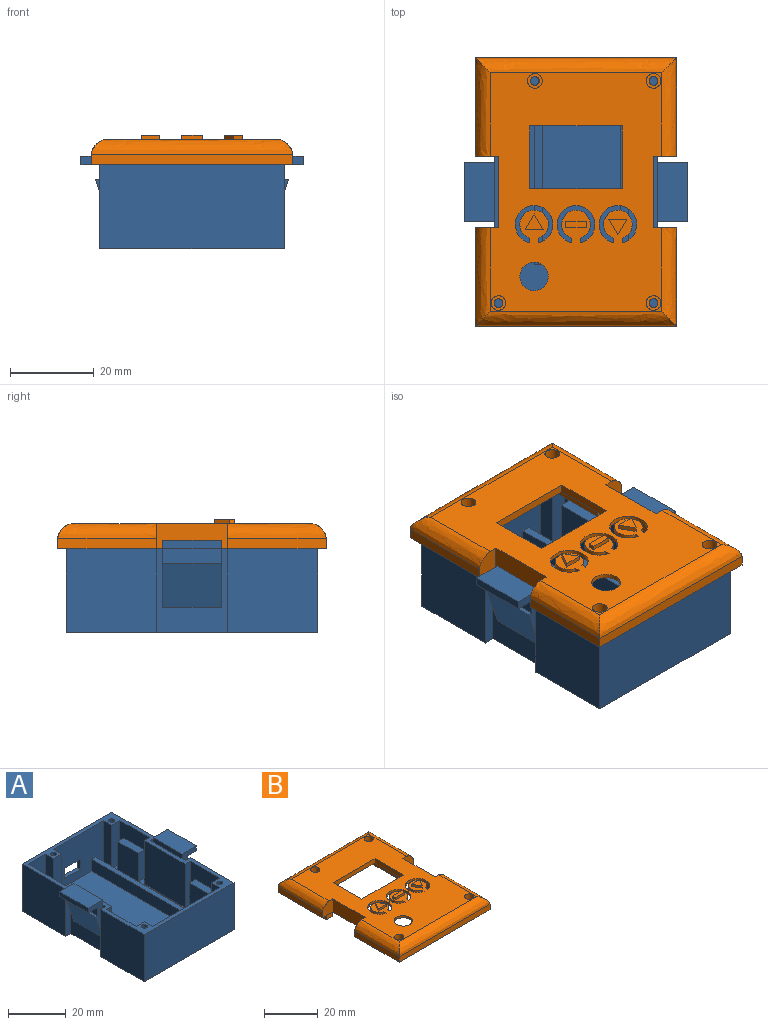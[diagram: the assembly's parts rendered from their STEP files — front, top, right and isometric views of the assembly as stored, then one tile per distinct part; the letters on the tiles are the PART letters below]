
ASSEMBLY  parts=2 mates=1
PART A: 93 faces, bbox 53x60x22 mm
  f0: plane 6x5mm, normal (0,1,0), area 30mm2, adj f2,f9,f73,f91
  f1: plane 8x5mm, normal (0,-1,0), area 40mm2, adj f2,f9,f77,f91
  f2: plane 45.7x8mm, normal (0,0,1), area 103.4mm2, adj f0,f1,f6,f73,f77,f91
  f3: plane 18.5x14.5mm, normal (-1,0,0), area 148.3mm2, adj f9,f18,f34,f56,f83,f84,f86
  f4: plane 18.5x14.5mm, normal (-1,0,0), area 148.2mm2, adj f9,f18,f35,f54,f79,f80,f82
  f5: plane 18.5x4mm, normal (0,-1,0), area 64mm2, adj f9,f18,f59,f60,f75,f78
  f6: plane 24.5x18.5mm, normal (0,-1,0), area 410.9mm2, adj f2,f9,f18,f53,f59,f69,f70,f71
  f7: plane 44x20mm, normal (0,1,0), area 847.7mm2, adj f17,f18,f21,f23,f69,f70,f71,f72
  f8: plane 20x8.5mm, normal (0,-1,0), area 164.7mm2, adj f9,f17,f18,f30,f38,f39,f60
  f9: plane 57x41mm, normal (0,0,1), area 1808mm2, adj f0,f1,f3,f4,f5,f6,f8,f10
  f10: plane 18.5x14.5mm, normal (1,0,0), area 148.3mm2, adj f9,f18,f31,f58,f87,f89,f90
  f11: plane 33x18.5mm, normal (0,1,0), area 610.5mm2, adj f9,f18,f55,f57
  f12: plane 14x2mm, normal (-1,0,0), area 28mm2, adj f13,f14,f47,f49
  f13: plane 16x7mm, normal (0,-1,0), area 41.1mm2, adj f12,f25,f47,f48,f49,f50,f51,f52
  f14: plane 16x7mm, normal (0,1,0), area 41.1mm2, adj f12,f25,f47,f48,f49,f50,f51,f52
  f15: plane 16x7mm, normal (0,-1,0), area 41.1mm2, adj f29,f40,f41,f42,f43,f44,f45,f46
  f16: plane 16x7mm, normal (0,1,0), area 41.1mm2, adj f29,f40,f41,f42,f43,f44,f45,f46
  f17: plane 60x44mm, normal (0,0,-1), area 2480mm2, adj f7,f8,f19,f20,f21,f22,f23,f24
  f18: plane 60x44mm, normal (0,0,1), area 368.1mm2, adj f3,f4,f5,f6,f7,f8,f10,f11
  f19: plane 21.5x20mm, normal (-1,0,0), area 430mm2, adj f17,f18,f22,f24
  f20: plane 21.5x20mm, normal (1,0,0), area 430mm2, adj f17,f18,f22,f27
  f21: plane 21.5x20mm, normal (-1,0,0), area 430mm2, adj f7,f17,f18,f26
  f22: plane 44x20mm, normal (0,-1,0), area 880mm2, adj f17,f18,f19,f20
  f23: plane 21.5x20mm, normal (1,0,0), area 430mm2, adj f7,f17,f18,f28
  f24: plane 20x2.5mm, normal (0,1,0), area 50mm2, adj f17,f18,f19,f25
  f25: plane 20x17mm, normal (-1,0,0), area 144mm2, adj f13,f14,f17,f18,f24,f26,f50
  f26: plane 20x2.5mm, normal (0,-1,0), area 50mm2, adj f17,f18,f21,f25
  f27: plane 20x2.5mm, normal (0,1,0), area 50mm2, adj f17,f18,f20,f29
  f28: plane 20x2.5mm, normal (0,-1,0), area 50mm2, adj f17,f18,f23,f29
  f29: plane 20x17mm, normal (1,0,0), area 144mm2, adj f15,f16,f17,f18,f27,f28,f46
  f30: plane 18.5x18.5mm, normal (1,0,0), area 342.3mm2, adj f8,f9,f18,f33
  f31: plane 18.5x2.5mm, normal (0,-1,0), area 46.3mm2, adj f9,f10,f18,f32
  f32: plane 20x18.5mm, normal (1,0,0), area 370mm2, adj f9,f18,f31,f33
  f33: plane 18.5x2.5mm, normal (0,1,0), area 46.3mm2, adj f9,f18,f30,f32
  f34: plane 18.5x2.5mm, normal (0,-1,0), area 46.3mm2, adj f3,f9,f18,f36
  f35: plane 18.5x2.5mm, normal (0,1,0), area 46.3mm2, adj f4,f9,f18,f36
  f36: plane 20x18.5mm, normal (-1,0,0), area 370mm2, adj f9,f18,f34,f35
  f37: plane 5x1.5mm, normal (0,1,0), area 7.5mm2, adj f9,f17,f38,f39
  f38: plane 15x1.5mm, normal (1,0,0), area 22.5mm2, adj f8,f9,f17,f37
  f39: plane 15x1.5mm, normal (-1,0,0), area 22.5mm2, adj f8,f9,f17,f37
  f40: plane 14x2mm, normal (-1,0,0), area 28mm2, adj f15,f16,f18,f41
  f41: plane 14x7mm, normal (0,0,1), area 98mm2, adj f15,f16,f40,f42
  f42: plane 14x2mm, normal (1,0,0), area 28mm2, adj f15,f16,f41,f43
  f43: plane 14x4.5mm, normal (0,0,-1), area 63mm2, adj f15,f16,f42,f44
  f44: plane 14x3.5mm, normal (1,0,0), area 49mm2, adj f15,f16,f43,f45
  f45: plane 14x1mm, normal (0,0,1), area 14mm2, adj f15,f16,f44,f46
  f46: plane 14x10.5mm, normal (0.95,0,-0.32), area 155mm2, adj f15,f16,f29,f45
  f47: plane 14x7mm, normal (0,0,1), area 98mm2, adj f12,f13,f14,f48
  f48: plane 14x2mm, normal (1,0,0), area 28mm2, adj f13,f14,f18,f47
  f49: plane 14x4.5mm, normal (0,0,-1), area 63mm2, adj f12,f13,f14,f52
  f50: plane 14x10.5mm, normal (-0.95,0,-0.32), area 155mm2, adj f13,f14,f25,f51
  f51: plane 14x1mm, normal (0,0,1), area 14mm2, adj f13,f14,f50,f52
  f52: plane 14x3.5mm, normal (-1,0,0), area 49mm2, adj f13,f14,f49,f51
  f53: plane 18.5x4mm, normal (-1,0,0), area 74mm2, adj f6,f9,f18,f54
  f54: plane 18.5x4mm, normal (0,-1,0), area 74mm2, adj f4,f9,f18,f53
  f55: plane 18.5x4mm, normal (-1,0,0), area 74mm2, adj f9,f11,f18,f56
  f56: plane 18.5x4mm, normal (0,1,0), area 74mm2, adj f3,f9,f18,f55
  f57: plane 18.5x4mm, normal (1,0,0), area 74mm2, adj f9,f11,f18,f58
  f58: plane 18.5x4mm, normal (0,1,0), area 74mm2, adj f9,f10,f18,f57
  f59: plane 43.7x18.5mm, normal (1,0,0), area 272.5mm2, adj f5,f6,f9,f18,f74,f78
  f60: plane 18.5x4mm, normal (-1,0,0), area 74mm2, adj f5,f8,f9,f18
  f61: cylinder r=1.05mm len=15mm, axis (0,0,1), area 99mm2, adj f18,f62
  f62: plane 2.1x2.1mm, normal (0,0,1), area 3.5mm2, adj f61
  f63: cylinder r=1.05mm len=15mm, axis (0,0,1), area 99mm2, adj f18,f64
  f64: plane 2.1x2.1mm, normal (0,0,1), area 3.5mm2, adj f63
  f65: cylinder r=1.05mm len=15mm, axis (0,0,1), area 99mm2, adj f18,f66
  f66: plane 2.1x2.1mm, normal (0,0,1), area 3.5mm2, adj f65
  f67: cylinder r=1.05mm len=15mm, axis (0,0,1), area 99mm2, adj f18,f68
  f68: plane 2.1x2.1mm, normal (0,0,1), area 3.5mm2, adj f67
  f69: plane 4.2x1.5mm, normal (1,0,0), area 6.3mm2, adj f6,f7,f70,f71
  f70: plane 7.7x1.5mm, normal (0,0,-1), area 11.5mm2, adj f6,f7,f69,f72
  f71: plane 7.7x1.5mm, normal (0,0,1), area 11.5mm2, adj f6,f7,f69,f72
  f72: plane 4.2x1.5mm, normal (-1,0,0), area 6.3mm2, adj f6,f7,f70,f71
  f73: plane 43.7x5mm, normal (-1,0,0), area 218.5mm2, adj f0,f2,f6,f9
  f74: plane 6.6x5mm, normal (0,1,0), area 33mm2, adj f9,f59,f78,f92
  f75: plane 41.7x5mm, normal (-1,0,0), area 208.5mm2, adj f5,f9,f76,f78
  f76: plane 8.6x5mm, normal (0,-1,0), area 43mm2, adj f9,f75,f78,f92
  f77: plane 45.7x5mm, normal (1,0,0), area 228.5mm2, adj f1,f2,f6,f9
  f78: plane 41.7x8.6mm, normal (0,0,1), area 96.6mm2, adj f5,f59,f74,f75,f76,f92
  f79: plane 12x3mm, normal (0,-1,0), area 36mm2, adj f4,f9,f81,f82
  f80: plane 12x3mm, normal (0,1,0), area 36mm2, adj f4,f9,f81,f82
  f81: plane 12x10mm, normal (-1,0,0), area 120mm2, adj f9,f79,f80,f82
  f82: plane 10x3mm, normal (0,0,1), area 30mm2, adj f4,f79,f80,f81
  f83: plane 12x3mm, normal (0,-1,0), area 36mm2, adj f3,f9,f85,f86
  f84: plane 12x3mm, normal (0,1,0), area 36mm2, adj f3,f9,f85,f86
  f85: plane 12x10mm, normal (-1,0,0), area 120mm2, adj f9,f83,f84,f86
  f86: plane 10x3mm, normal (0,0,1), area 30mm2, adj f3,f83,f84,f85
  f87: plane 12x3mm, normal (0,-1,0), area 36mm2, adj f9,f10,f88,f90
  f88: plane 12x10mm, normal (1,0,0), area 120mm2, adj f9,f87,f89,f90
  f89: plane 12x3mm, normal (0,1,0), area 36mm2, adj f9,f10,f88,f90
  f90: plane 10x3mm, normal (0,0,1), area 30mm2, adj f10,f87,f88,f89
  f91: plane 5x2mm, normal (-1,0,0), area 10mm2, adj f0,f1,f2,f9
  f92: plane 5x2mm, normal (1,0,0), area 10mm2, adj f9,f74,f76,f78
PART B: 131 faces, bbox 53.2x66.8x10.9 mm
  f0: plane 50.6x34.6mm, normal (0,0,-1), area 1144.6mm2, adj f53,f54,f55,f56,f57,f58,f59,f60
  f1: plane 2.5x0.24mm, normal (0,0,-1), area 0.4mm2, adj f85,f103
  f2: plane 2.5x0.24mm, normal (0,0,-1), area 0.4mm2, adj f85,f101
  f3: plane 6.32x2.15mm, normal (0,0,-1), area 9.9mm2, adj f85,f102
  f4: plane 2.5x0.24mm, normal (0,0,-1), area 0.4mm2, adj f82,f98
  f5: plane 2.5x0.24mm, normal (0,0,-1), area 0.4mm2, adj f82,f96
  f6: plane 6.32x2.15mm, normal (0,0,-1), area 9.9mm2, adj f82,f97
  f7: plane 2.5x0.24mm, normal (0,0,-1), area 0.4mm2, adj f89,f93
  f8: plane 2.5x0.24mm, normal (0,0,-1), area 0.4mm2, adj f89,f91
  f9: plane 6.32x2.15mm, normal (0,0,-1), area 9.9mm2, adj f89,f92
  f10: plane 57x41mm, normal (0,0,1), area 1765.2mm2, adj f36,f37,f38,f39,f40,f41,f68,f70
  f11: cylinder r=1.05mm len=2.1mm, axis (0,0,-1), area 6.6mm2, adj f19,f73
  f12: cylinder r=1.05mm len=2.1mm, axis (0,0,-1), area 6.6mm2, adj f19,f71
  f13: cylinder r=1.05mm len=2.1mm, axis (0,0,-1), area 6.6mm2, adj f19,f69
  f14: cylinder r=1.05mm len=2.1mm, axis (0,0,-1), area 6.6mm2, adj f19,f67
  f15: plane 3.5x3.1mm, normal (-1,0,0), area 10.9mm2, adj f19,f29,f45,f64
  f16: plane 3.5x3.1mm, normal (0,1,0), area 10.9mm2, adj f19,f25,f47,f53
  f17: plane 3.5x3.1mm, normal (1,0,0), area 10.9mm2, adj f19,f26,f50,f57
  f18: plane 3.5x3.1mm, normal (0,-1,0), area 10.9mm2, adj f19,f27,f52,f54
  f19: plane 64x48mm, normal (0,0,-1), area 746.6mm2, adj f11,f12,f13,f14,f15,f16,f17,f18
  f20: plane 3.5x3.1mm, normal (0,-1,0), area 10.9mm2, adj f19,f28,f42,f54
  f21: plane 3.5x3.1mm, normal (0,-1,0), area 10.9mm2, adj f19,f25,f47,f53
  f22: plane 3.5x3.1mm, normal (0,1,0), area 10.9mm2, adj f19,f24,f48,f53
  f23: plane 3.5x3.1mm, normal (0,1,0), area 10.9mm2, adj f19,f27,f52,f54
  f24: plane 14.2x3.1mm, normal (0,0,-1), area 44mm2, adj f22,f48,f49,f53
  f25: plane 14.2x3.1mm, normal (0,0,-1), area 44mm2, adj f16,f21,f47,f53
  f26: plane 32.6x3.1mm, normal (0,0,-1), area 101.1mm2, adj f17,f50,f51,f57
  f27: plane 14.2x3.1mm, normal (0,0,-1), area 44mm2, adj f18,f23,f52,f54
  f28: plane 18.3x8.5mm, normal (0,0,-1), area 73.5mm2, adj f20,f42,f43,f44,f54,f60
  f29: plane 24x3.1mm, normal (0,0,-1), area 74.4mm2, adj f15,f45,f46,f64
  f30: plane 23.5x2.5mm, normal (1,0,0), area 58.8mm2, adj f19,f32,f36,f124
  f31: plane 23.5x2.5mm, normal (-1,0,0), area 58.8mm2, adj f19,f32,f39,f126
  f32: plane 48x2.5mm, normal (0,-1,0), area 120mm2, adj f19,f30,f31,f125
  f33: plane 23.5x2.5mm, normal (1,0,0), area 58.7mm2, adj f19,f34,f37,f127
  f34: plane 48x2.5mm, normal (0,1,0), area 120mm2, adj f19,f33,f35,f129
  f35: plane 23.5x2.5mm, normal (-1,0,0), area 58.7mm2, adj f19,f34,f41,f128
  f36: plane 6.43x5.93mm, normal (0,1,0), area 29.7mm2, adj f10,f19,f30,f38,f124
  f37: plane 6.43x5.93mm, normal (0,-1,0), area 29.7mm2, adj f10,f19,f33,f38,f127
  f38: plane 17x6mm, normal (1,0,0), area 102mm2, adj f10,f19,f36,f37
  f39: plane 6.43x5.93mm, normal (0,1,0), area 29.7mm2, adj f10,f19,f31,f40,f126
  f40: plane 17x6mm, normal (-1,0,0), area 102mm2, adj f10,f19,f39,f41
  f41: plane 6.43x5.93mm, normal (0,-1,0), area 29.7mm2, adj f10,f19,f35,f40,f128
  f42: plane 18.3x3.5mm, normal (-1,0,0), area 64.1mm2, adj f19,f20,f28,f43
  f43: plane 8.5x3.5mm, normal (0,1,0), area 29.8mm2, adj f19,f28,f42,f44
  f44: plane 3.5x3.1mm, normal (1,0,0), area 10.9mm2, adj f19,f28,f43,f60
  f45: plane 24x3.5mm, normal (0,1,0), area 84mm2, adj f15,f19,f29,f46
  f46: plane 3.5x3.1mm, normal (1,0,0), area 10.9mm2, adj f19,f29,f45,f64
  f47: plane 14.2x3.5mm, normal (1,0,0), area 49.7mm2, adj f16,f19,f21,f25
  f48: plane 14.2x3.5mm, normal (1,0,0), area 49.7mm2, adj f19,f22,f24,f49
  f49: plane 3.5x3.1mm, normal (0,-1,0), area 10.9mm2, adj f19,f24,f48,f53
  f50: plane 32.6x3.5mm, normal (0,-1,0), area 114.1mm2, adj f17,f19,f26,f51
  f51: plane 3.5x3.1mm, normal (-1,0,0), area 10.9mm2, adj f19,f26,f50,f57
  f52: plane 14.2x3.5mm, normal (-1,0,0), area 49.7mm2, adj f18,f19,f23,f27
  f53: plane 48.6x8.5mm, normal (-1,0,0), area 342.4mm2, adj f0,f16,f19,f21,f22,f24,f25,f49
  f54: plane 49.6x8.5mm, normal (1,0,0), area 350.9mm2, adj f0,f18,f19,f20,f23,f27,f28,f59
  f55: plane 5x1mm, normal (0,1,0), area 5mm2, adj f0,f19,f53,f56
  f56: plane 5x1mm, normal (-1,0,0), area 5mm2, adj f0,f19,f55,f57
  f57: plane 32.6x8.5mm, normal (0,1,0), area 277.1mm2, adj f0,f17,f26,f51,f56,f58
  f58: plane 5x1mm, normal (1,0,0), area 5mm2, adj f0,f19,f57,f59
  f59: plane 5x1mm, normal (0,1,0), area 5mm2, adj f0,f19,f54,f58
  f60: plane 8.5x5.4mm, normal (0,-1,0), area 45.9mm2, adj f0,f28,f44,f54,f61
  f61: plane 5x1mm, normal (-1,0,0), area 5mm2, adj f0,f19,f60,f62
  f62: plane 5x4.2mm, normal (0,-1,0), area 21mm2, adj f0,f19,f61,f63
  f63: plane 5x1mm, normal (1,0,0), area 5mm2, adj f0,f19,f62,f64
  f64: plane 24x8.5mm, normal (0,-1,0), area 204mm2, adj f0,f15,f29,f46,f63,f65
  f65: plane 5x1mm, normal (-1,0,0), area 5mm2, adj f0,f19,f64,f66
  f66: plane 5x1mm, normal (0,-1,0), area 5mm2, adj f0,f19,f53,f65
  f67: plane 3.5x3.5mm, normal (0,0,1), area 6.2mm2, adj f14,f68
  f68: cylinder r=1.75mm len=5mm, axis (0,0,1), area 55mm2, adj f10,f67
  f69: plane 3.5x3.5mm, normal (0,0,1), area 6.2mm2, adj f13,f70
  f70: cylinder r=1.75mm len=5mm, axis (0,0,1), area 55mm2, adj f10,f69
  f71: plane 3.5x3.5mm, normal (0,0,1), area 6.2mm2, adj f12,f72
  f72: cylinder r=1.75mm len=5mm, axis (0,0,1), area 55mm2, adj f10,f71
  f73: plane 3.5x3.5mm, normal (0,0,1), area 6.2mm2, adj f11,f74
  f74: cylinder r=1.75mm len=5mm, axis (0,0,1), area 55mm2, adj f10,f73
  f75: plane 22x2mm, normal (0,-1,0), area 44mm2, adj f10,f76,f78,f123
  f76: plane 15x2mm, normal (-1,0,0), area 30mm2, adj f10,f75,f77,f123
  f77: plane 22x2mm, normal (0,1,0), area 44mm2, adj f10,f76,f78,f123
  f78: plane 15x2mm, normal (1,0,0), area 30mm2, adj f10,f75,f77,f123
  f79: plane 1.14x1mm, normal (-1,0,0), area 1.1mm2, adj f0,f10,f80,f82
  f80: cylinder r=4.5mm len=9mm, axis (0,0,-1), area 26.3mm2, adj f0,f10,f79,f81
  f81: plane 1.14x1mm, normal (1,0,0), area 1.1mm2, adj f0,f10,f80,f82
  f82: cylinder r=3.4mm len=6.8mm, axis (0,0,-1), area 19.3mm2, adj f0,f4,f5,f6,f10,f79,f81
  f83: cylinder r=4.5mm len=9mm, axis (0,0,-1), area 26.3mm2, adj f0,f10,f84,f86
  f84: plane 1.14x1mm, normal (1,0,0), area 1.1mm2, adj f0,f10,f83,f85
  f85: cylinder r=3.4mm len=6.8mm, axis (0,0,-1), area 19.3mm2, adj f0,f1,f2,f3,f10,f84,f86
  f86: plane 1.14x1mm, normal (-1,0,0), area 1.1mm2, adj f0,f10,f83,f85
  f87: cylinder r=4.5mm len=9mm, axis (0,0,-1), area 26.3mm2, adj f0,f10,f88,f90
  f88: plane 1.14x1mm, normal (1,0,0), area 1.1mm2, adj f0,f10,f87,f89
  f89: cylinder r=3.4mm len=6.8mm, axis (0,0,-1), area 19.3mm2, adj f0,f7,f8,f9,f10,f88,f90
  f90: plane 1.14x1mm, normal (-1,0,0), area 1.1mm2, adj f0,f10,f87,f89
  f91: plane 2.5x2mm, normal (-1,0,0), area 5mm2, adj f8,f92,f94,f95
  f92: plane 6.32x2mm, normal (0,1,0), area 12.6mm2, adj f9,f91,f93,f95
  f93: plane 2.5x2mm, normal (1,0,0), area 5mm2, adj f7,f92,f94,f95
  f94: plane 6.32x2mm, normal (0,-1,0), area 12.6mm2, adj f0,f91,f93,f95
  f95: plane 6.32x2.5mm, normal (0,0,-1), area 15.8mm2, adj f91,f92,f93,f94
  f96: plane 2.5x2mm, normal (-1,0,0), area 5mm2, adj f5,f97,f99,f100
  f97: plane 6.32x2mm, normal (0,1,0), area 12.6mm2, adj f6,f96,f98,f100
  f98: plane 2.5x2mm, normal (1,0,0), area 5mm2, adj f4,f97,f99,f100
  f99: plane 6.32x2mm, normal (0,-1,0), area 12.6mm2, adj f0,f96,f98,f100
  f100: plane 6.32x2.5mm, normal (0,0,-1), area 15.8mm2, adj f96,f97,f98,f99
  f101: plane 2.5x2mm, normal (-1,0,0), area 5mm2, adj f2,f102,f104,f105
  f102: plane 6.32x2mm, normal (0,1,0), area 12.6mm2, adj f3,f101,f103,f105
  f103: plane 2.5x2mm, normal (1,0,0), area 5mm2, adj f1,f102,f104,f105
  f104: plane 6.32x2mm, normal (0,-1,0), area 12.6mm2, adj f0,f101,f103,f105
  f105: plane 6.32x2.5mm, normal (0,0,-1), area 15.8mm2, adj f101,f102,f103,f104
  f106: plane 3.75x2.17mm, normal (0.87,-0.5,0), area 4.3mm2, adj f10,f107,f108,f109
  f107: plane 4.33x1mm, normal (0,1,0), area 4.3mm2, adj f10,f106,f108,f109
  f108: plane 3.75x2.17mm, normal (-0.87,-0.5,0), area 4.3mm2, adj f10,f106,f107,f109
  f109: plane 4.33x3.75mm, normal (0,0,1), area 8.1mm2, adj f106,f107,f108
  f110: plane 4.33x1mm, normal (0,-1,0), area 4.3mm2, adj f10,f111,f112,f113
  f111: plane 3.75x2.17mm, normal (0.87,0.5,0), area 4.3mm2, adj f10,f110,f112,f113
  f112: plane 3.75x2.17mm, normal (-0.87,0.5,0), area 4.3mm2, adj f10,f110,f111,f113
  f113: plane 4.33x3.75mm, normal (0,0,1), area 8.1mm2, adj f110,f111,f112
  f114: plane 5x1mm, normal (0,1,0), area 5mm2, adj f10,f115,f117,f118
  f115: plane 1.5x1mm, normal (-1,0,0), area 1.5mm2, adj f10,f114,f116,f118
  f116: plane 5x1mm, normal (0,-1,0), area 5mm2, adj f10,f115,f117,f118
  f117: plane 1.5x1mm, normal (1,0,0), area 1.5mm2, adj f10,f114,f116,f118
  f118: plane 5x1.5mm, normal (0,0,1), area 7.5mm2, adj f114,f115,f116,f117
  f119: plane 17x1mm, normal (1,0,0), area 17mm2, adj f0,f120,f122,f123
  f120: plane 24x1mm, normal (0,-1,0), area 24mm2, adj f0,f119,f121,f123
  f121: plane 17x1mm, normal (-1,0,0), area 17mm2, adj f0,f120,f122,f123
  f122: plane 24x1mm, normal (0,1,0), area 24mm2, adj f0,f119,f121,f123
  f123: plane 24x17mm, normal (0,0,-1), area 78mm2, adj f75,f76,f77,f78,f119,f120,f121,f122
  f124: bspline ~25.85x3.5mm, area 116mm2, adj f10,f30,f36,f125
  f125: bspline ~52.8x3.5mm, area 237.4mm2, adj f10,f32,f124,f126
  f126: bspline ~25.85x3.5mm, area 116mm2, adj f10,f31,f39,f125
  f127: bspline ~25.85x3.5mm, area 116mm2, adj f10,f33,f37,f129
  f128: bspline ~25.85x3.5mm, area 116mm2, adj f10,f35,f41,f129
  f129: bspline ~52.8x3.5mm, area 237.4mm2, adj f10,f34,f127,f128
  f130: cylinder r=3.4mm len=6.8mm, axis (0,0,-1), area 21.4mm2, adj f0,f10
PLACE A t=(-0.58,4.6,6.62)mm
PLACE B t=(-0.58,4.6,26.62)mm
MATE fastened B.f13 <-> A.f65  axis (0,0,-1) through (17.92,-21.9,26.62)mm
